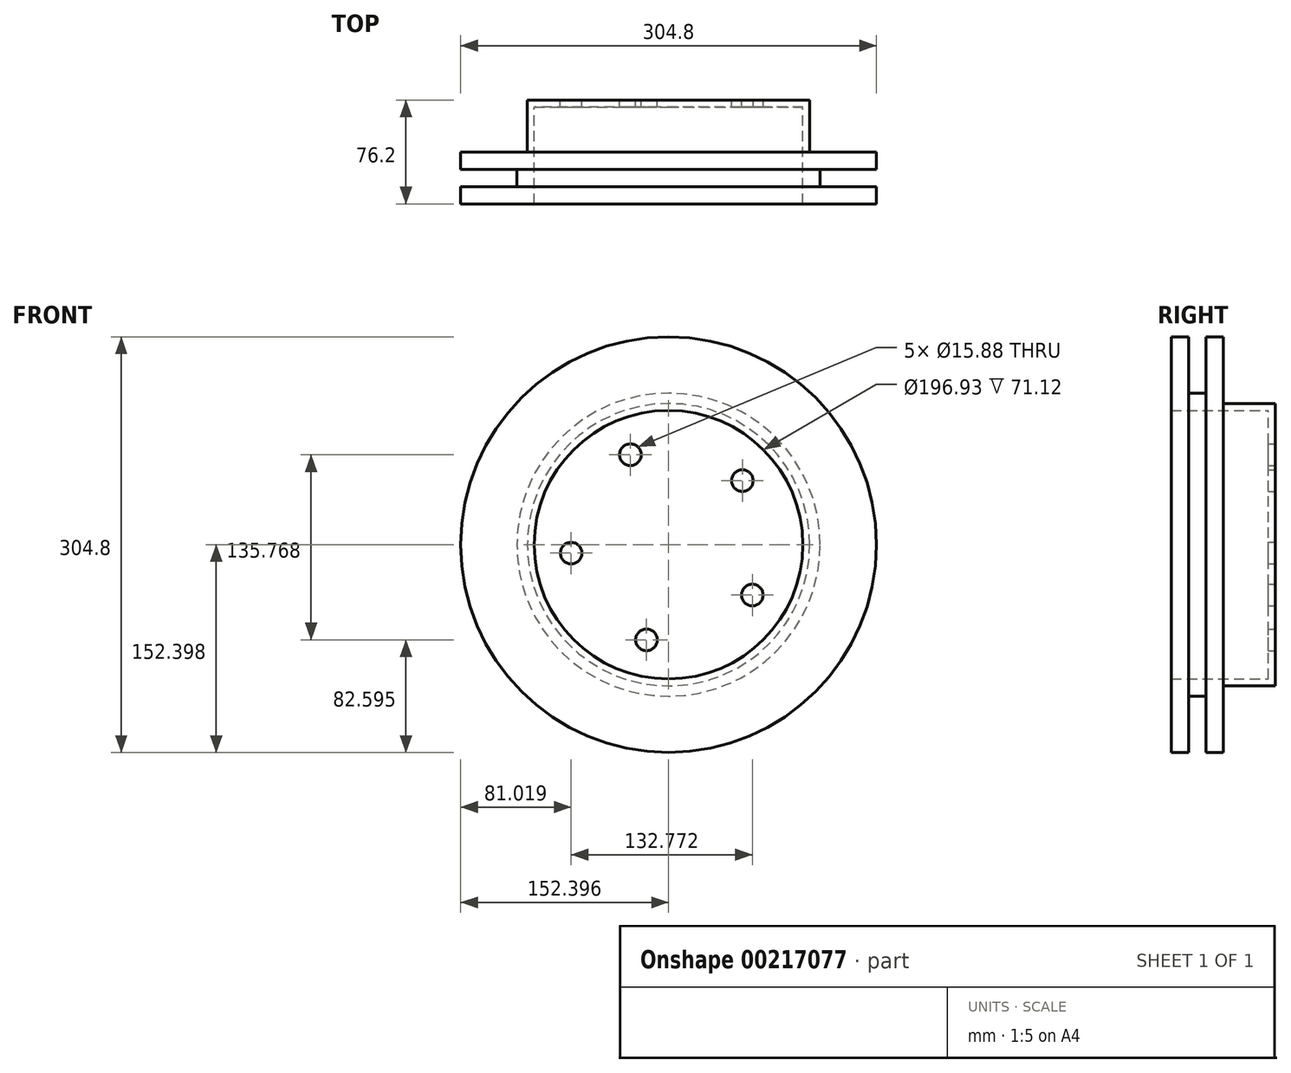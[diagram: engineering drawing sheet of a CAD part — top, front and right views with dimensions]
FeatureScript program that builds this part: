
annotation { "Feature Type Name" : "Feature", "Feature Type Description" : "" }
export const myFeature = defineFeature(function(context is Context, id is Id, definition is map)
    precondition{}
    {
        {
            var Q0;
            Q0=qCreatedBy(makeId("Front.planeOp"),FACE);
            var sketch = newSketch(context, id + "F0", { "sketchPlane" : qUnion([Q0])});
            skCircle(sketch, "E0", {"center": v(-72.94, 72.91) * mm, "radius": 7.94 * mm});
            skCircle(sketch, "E1", {"center": v(9.12, 53.93) * mm, "radius": 7.94 * mm});
            skCircle(sketch, "E2", {"center": v(-116.35, 0.74) * mm, "radius": 7.94 * mm});
            skCircle(sketch, "E3", {"center": v(-61.12, -62.86) * mm, "radius": 7.94 * mm});
            skCircle(sketch, "E4", {"center": v(16.42, -29.99) * mm, "radius": 7.94 * mm});
            skLineSegment(sketch, "E5", {"start": v(16.42, -29.99) * mm, "end": v(16.42, -29.99) * mm, "construction": true});
            skLineSegment(sketch, "E6", {"start": v(16.42, -29.99) * mm, "end": v(16.42, -29.98) * mm, "construction": true});
            skLineSegment(sketch, "E7.2", {"start": v(16.42, -29.98) * mm, "end": v(16.42, -29.99) * mm});
            skCircle(sketch, "E8", {"center": v(-44.97, 6.95) * mm, "radius": 103.54 * mm});
            skLineSegment(sketch, "E9.trimOffspring", {"start": v(58.4, 0.98) * mm, "end": v(91.83, 0.98) * mm, "construction": true});
            skSolve(sketch);
        }
        {
            var Q0;
            Q0=makeQuery(id+"F0.imprint","IMPRINT",FACE,{"disambiguationData":[TD([[makeQuery(id+"F0.imprint","IMPRINT",EDGE,{"derivedFrom":sQuery(id+"F0.wireOp",EDGE,"E0")}),-1.0]])]});
            var Q1;
            {var subQ0=sQuery(id+"F0.wireOp",EDGE,"7bd9e01d-88c7-40c8-ba76-cef98e0b3f60.trimOffspring");Q1=makeQuery(id+"F0.imprint","IMPRINT",FACE,{"disambiguationData":[TD([[makeQuery(id+"F0.imprint","IMPRINT",EDGE,{"derivedFrom":subQ0}),1.0]])]});}
            var Q2;
            Q2=makeQuery(id+"F0.imprint","IMPRINT",FACE,{"disambiguationData":[TD([[makeQuery(id+"F0.imprint","IMPRINT",EDGE,{"derivedFrom":sQuery(id+"F0.wireOp",EDGE,"E1")}),1.0]])]});
            var Q3;
            Q3=makeQuery(id+"F0.imprint","IMPRINT",FACE,{"disambiguationData":[TD([[makeQuery(id+"F0.imprint","IMPRINT",EDGE,{"derivedFrom":sQuery(id+"F0.wireOp",EDGE,"E0")}),1.0]])]});
            var Q4;
            Q4=makeQuery(id+"F0.imprint","IMPRINT",FACE,{"disambiguationData":[TD([[makeQuery(id+"F0.imprint","IMPRINT",EDGE,{"derivedFrom":sQuery(id+"F0.wireOp",EDGE,"E2")}),1.0]])]});
            var Q5;
            Q5=makeQuery(id+"F0.imprint","IMPRINT",FACE,{"disambiguationData":[TD([[makeQuery(id+"F0.imprint","IMPRINT",EDGE,{"derivedFrom":sQuery(id+"F0.wireOp",EDGE,"E3")}),1.0]])]});
            var Q6;
            Q6=makeQuery(id+"F0.imprint","IMPRINT",FACE,{"disambiguationData":[TD([[makeQuery(id+"F0.imprint","IMPRINT",EDGE,{"derivedFrom":sQuery(id+"F0.wireOp",EDGE,"E4")}),1.0]])]});
            extrude(context, id + "F1", {"entities" : qUnion([Q0, Q1, Q2, Q3, Q4, Q5, Q6]), "depth" : 38.1 * mm});
        }
        {
            var Q0;
            Q0=makeQuery(id+"F1.opExtrude","CAP_FACE",FACE,{"disambiguationData":[OSD([sQuery(id+"F0.wireOp",EDGE,"E8")])],"isStart":false});
            shell(context, id + "F2", {"entities" : qUnion([Q0]), "thickness" : 5.08 * mm});
        }
        {
            var Q0;
            Q0=makeQuery(id+"F0.imprint","IMPRINT",FACE,{"disambiguationData":[TD([[makeQuery(id+"F0.imprint","IMPRINT",EDGE,{"derivedFrom":sQuery(id+"F0.wireOp",EDGE,"E3")}),1.0]])]});
            var Q1;
            Q1=makeQuery(id+"F0.imprint","IMPRINT",FACE,{"disambiguationData":[TD([[makeQuery(id+"F0.imprint","IMPRINT",EDGE,{"derivedFrom":sQuery(id+"F0.wireOp",EDGE,"E2")}),1.0]])]});
            var Q2;
            Q2=makeQuery(id+"F0.imprint","IMPRINT",FACE,{"disambiguationData":[TD([[makeQuery(id+"F0.imprint","IMPRINT",EDGE,{"derivedFrom":sQuery(id+"F0.wireOp",EDGE,"E0")}),1.0]])]});
            var Q3;
            Q3=makeQuery(id+"F0.imprint","IMPRINT",FACE,{"disambiguationData":[TD([[makeQuery(id+"F0.imprint","IMPRINT",EDGE,{"derivedFrom":sQuery(id+"F0.wireOp",EDGE,"E1")}),1.0]])]});
            var Q4;
            Q4=makeQuery(id+"F0.imprint","IMPRINT",FACE,{"disambiguationData":[TD([[makeQuery(id+"F0.imprint","IMPRINT",EDGE,{"derivedFrom":sQuery(id+"F0.wireOp",EDGE,"E4")}),1.0]])]});
            extrude(context, id + "F3", {"entities" : qUnion([Q0, Q1, Q2, Q3, Q4]), "operationType" : NewBodyOperationType.REMOVE, "endBound" : BoundingType.THROUGH_ALL, "depth" : 25.4 * mm});
        }
        {
            var Q0;
            Q0=makeQuery(id+"F1.opExtrude","CAP_FACE",FACE,{"disambiguationData":[OSD([sQuery(id+"F0.wireOp",EDGE,"E8")])],"isStart":false});
            var sketch = newSketch(context, id + "F4", { "sketchPlane" : qUnion([Q0])});
            skCircle(sketch, "E10", {"center": v(-44.97, 6.95) * mm, "radius": 152.4 * mm});
            skSolve(sketch);
        }
        {
            var Q0;
            {var subQ0=sQuery(id+"F0.wireOp",EDGE,"E8");var subQ1=makeQuery(id+"F1.opExtrude","CAP_EDGE",EDGE,{"disambiguationData":[OSD([subQ0])],"isStart":false});Q0=makeQuery(id+"F4.imprint","IMPRINT",FACE,{"disambiguationData":[TD([[makeQuery(id+"F4.imprint","IMPRINT",EDGE,{"derivedFrom":subQ1}),1.0]])]});}
            var Q1;
            Q1=makeQuery(id+"F4.imprint","IMPRINT",FACE,{"disambiguationData":[TD([[makeQuery(id+"F4.imprint","IMPRINT",EDGE,{"derivedFrom":sQuery(id+"F4.wireOp",EDGE,"E10")}),1.0]])]});
            extrude(context, id + "F5", {"entities" : qUnion([Q0, Q1]), "operationType" : NewBodyOperationType.ADD, "depth" : 38.1 * mm});
        }
        {
            var Q0;
            Q0=makeQuery(id+"F5.opExtrude","SWEPT_FACE",FACE,{"disambiguationData":[OSD([sQuery(id+"F4.wireOp",EDGE,"E10")])]});
            shell(context, id + "F6", {"entities" : qUnion([Q0]), "thickness" : 12.7 * mm});
        }
    });
